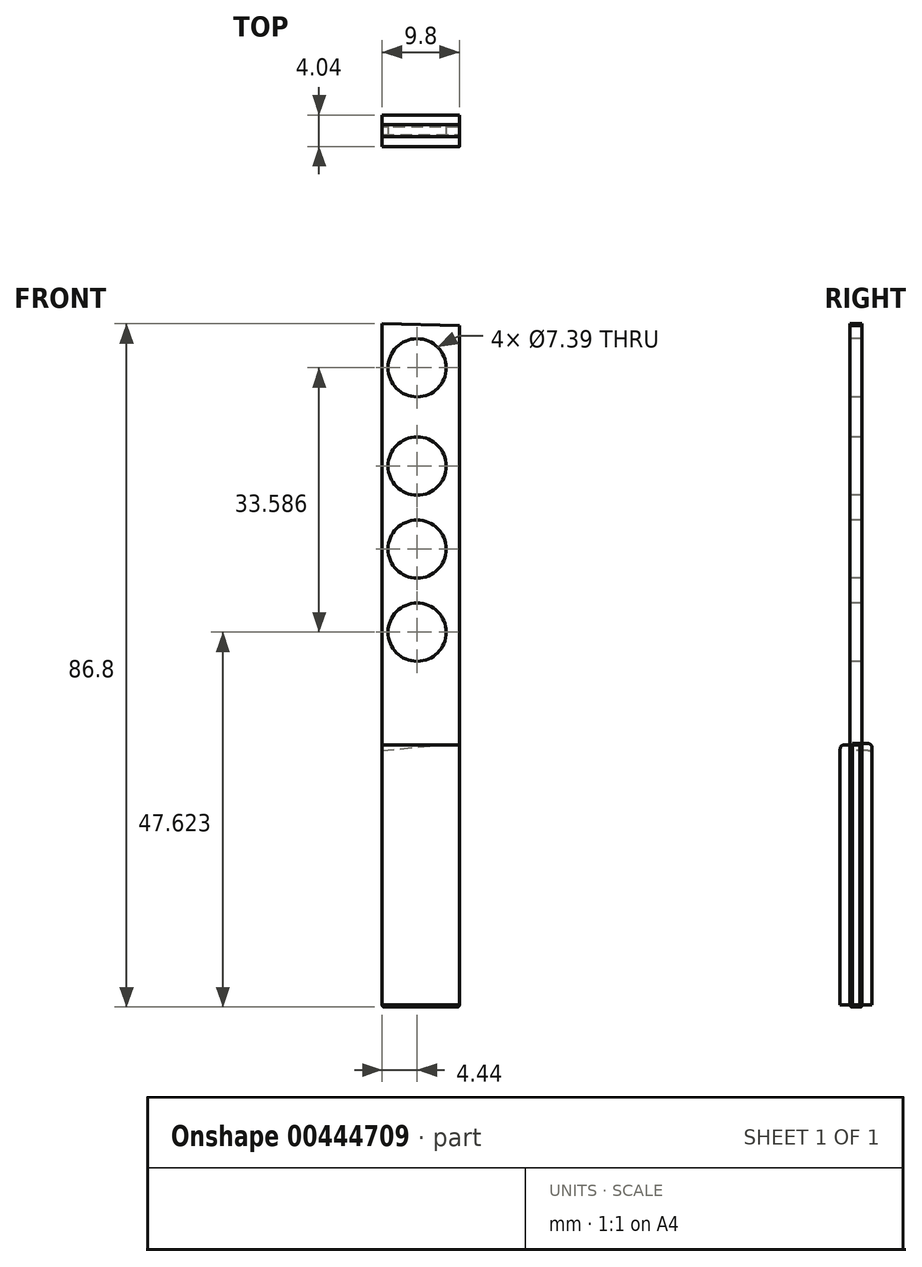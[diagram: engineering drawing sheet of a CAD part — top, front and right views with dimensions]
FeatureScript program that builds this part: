
annotation { "Feature Type Name" : "Feature", "Feature Type Description" : "" }
export const myFeature = defineFeature(function(context is Context, id is Id, definition is map)
    precondition{}
    {
        {
            var Q0;
            Q0=qCreatedBy(makeId("Front.planeOp"),FACE);
            var sketch = newSketch(context, id + "F0", { "sketchPlane" : qUnion([Q0])});
            skLineSegment(sketch, "E0", {"start": v(-4.44, 31.02) * mm, "end": v(-4.44, -55.78) * mm});
            skLineSegment(sketch, "E1", {"start": v(-4.44, -55.78) * mm, "end": v(5.36, -55.78) * mm});
            skLineSegment(sketch, "E2", {"start": v(5.36, -55.78) * mm, "end": v(5.36, 30.82) * mm});
            skLineSegment(sketch, "E3", {"start": v(5.36, 30.82) * mm, "end": v(-4.44, 31.02) * mm});
            skSolve(sketch);
        }
        {
            var Q0;
            Q0 = qSketchRegion(id + "F0", true);
            extrude(context, id + "F1", {"entities" : qUnion([Q0]), "depth" : 1.52 * mm});
        }
        {
            var Q0;
            Q0=makeQuery(id+"F1.opExtrude","SWEPT_FACE",FACE,{"disambiguationData":[OSD([sQuery(id+"F0.wireOp",EDGE,"E1")])]});
            fillet(context, id + "F2", {"entities" : qUnion([Q0]), "radius" : 0.25 * mm, "tangentPropagation" : true, "allowEdgeOverflow" : false});
        }
        {
            var Q0;
            Q0=makeQuery(id+"F1.opExtrude","CAP_FACE",FACE,{"disambiguationData":[OSD([sQuery(id+"F0.wireOp",EDGE,"E0"),sQuery(id+"F0.wireOp",EDGE,"E1"),sQuery(id+"F0.wireOp",EDGE,"E2"),sQuery(id+"F0.wireOp",EDGE,"E3")])],"isStart":false});
            var sketch = newSketch(context, id + "F3", { "sketchPlane" : qUnion([Q0])});
            skCircle(sketch, "E4", {"center": v(0, 25.43) * mm, "radius": 3.7 * mm});
            skCircle(sketch, "E5", {"center": v(0, 12.95) * mm, "radius": 3.7 * mm});
            skCircle(sketch, "E6", {"center": v(0, 2.4) * mm, "radius": 3.7 * mm});
            skCircle(sketch, "E7", {"center": v(0, -8.16) * mm, "radius": 3.7 * mm});
            skSolve(sketch);
        }
        {
            var Q0;
            Q0 = qSketchRegion(id + "F3", true);
            extrude(context, id + "F4", {"entities" : qUnion([Q0]), "operationType" : NewBodyOperationType.REMOVE, "endBound" : BoundingType.THROUGH_ALL, "oppositeDirection" : true, "depth" : 25.4 * mm});
        }
        {
            var Q0;
            Q0=makeQuery(id+"F1.opExtrude","CAP_FACE",FACE,{"disambiguationData":[OSD([sQuery(id+"F0.wireOp",EDGE,"E0"),sQuery(id+"F0.wireOp",EDGE,"E1"),sQuery(id+"F0.wireOp",EDGE,"E2"),sQuery(id+"F0.wireOp",EDGE,"E3")])],"isStart":false});
            var sketch = newSketch(context, id + "F5", { "sketchPlane" : qUnion([Q0])});
            skLineSegment(sketch, "E8", {"start": v(-4.44, -22.48) * mm, "end": v(-4.44, -55.52) * mm});
            skLineSegment(sketch, "E9", {"start": v(-4.44, -55.52) * mm, "end": v(5.36, -55.52) * mm});
            skLineSegment(sketch, "E10", {"start": v(5.36, -55.52) * mm, "end": v(5.36, -22.48) * mm});
            skLineSegment(sketch, "E11", {"start": v(5.36, -22.48) * mm, "end": v(-4.44, -22.48) * mm});
            skSolve(sketch);
        }
        {
            var Q0;
            Q0 = qSketchRegion(id + "F5", true);
            extrude(context, id + "F6", {"entities" : qUnion([Q0]), "endBound" : BoundingType.SYMMETRIC, "oppositeDirection" : true, "depth" : 2.5 * mm});
        }
        {
            var Q0;
            Q0=makeQuery(id+"F6.opExtrude","CAP_EDGE",EDGE,{"disambiguationData":[OSD([sQuery(id+"F5.wireOp",EDGE,"E11")])],"isStart":true});
            fillet(context, id + "F7", {"entities" : qUnion([Q0]), "radius" : 0.5 * mm, "tangentPropagation" : true, "allowEdgeOverflow" : false});
        }
        {
            var Q0;
            Q0=makeQuery(id+"F1.opExtrude","CAP_FACE",FACE,{"disambiguationData":[OSD([sQuery(id+"F0.wireOp",EDGE,"E0"),sQuery(id+"F0.wireOp",EDGE,"E1"),sQuery(id+"F0.wireOp",EDGE,"E2"),sQuery(id+"F0.wireOp",EDGE,"E3")])],"isStart":true});
            var sketch = newSketch(context, id + "F8", { "sketchPlane" : qUnion([Q0])});
            skLineSegment(sketch, "E12", {"start": v(-5.36, -22.3) * mm, "end": v(-5.36, -55.52) * mm});
            skLineSegment(sketch, "E13", {"start": v(-5.36, -55.52) * mm, "end": v(4.44, -55.52) * mm});
            skLineSegment(sketch, "E14", {"start": v(4.44, -55.52) * mm, "end": v(4.44, -23.17) * mm});
            skLineSegment(sketch, "E15", {"start": v(4.44, -23.17) * mm, "end": v(-5.36, -22.3) * mm});
            skSolve(sketch);
        }
        {
            var Q0;
            Q0 = qSketchRegion(id + "F8", true);
            extrude(context, id + "F9", {"entities" : qUnion([Q0]), "endBound" : BoundingType.SYMMETRIC, "depth" : 2.5 * mm});
        }
        {
            var Q0;
            Q0=makeQuery(id+"F9.opExtrude","CAP_EDGE",EDGE,{"disambiguationData":[OSD([sQuery(id+"F8.wireOp",EDGE,"E15")])],"isStart":false});
            fillet(context, id + "F10", {"entities" : qUnion([Q0]), "radius" : 0.5 * mm, "tangentPropagation" : true, "allowEdgeOverflow" : false});
        }
    });
